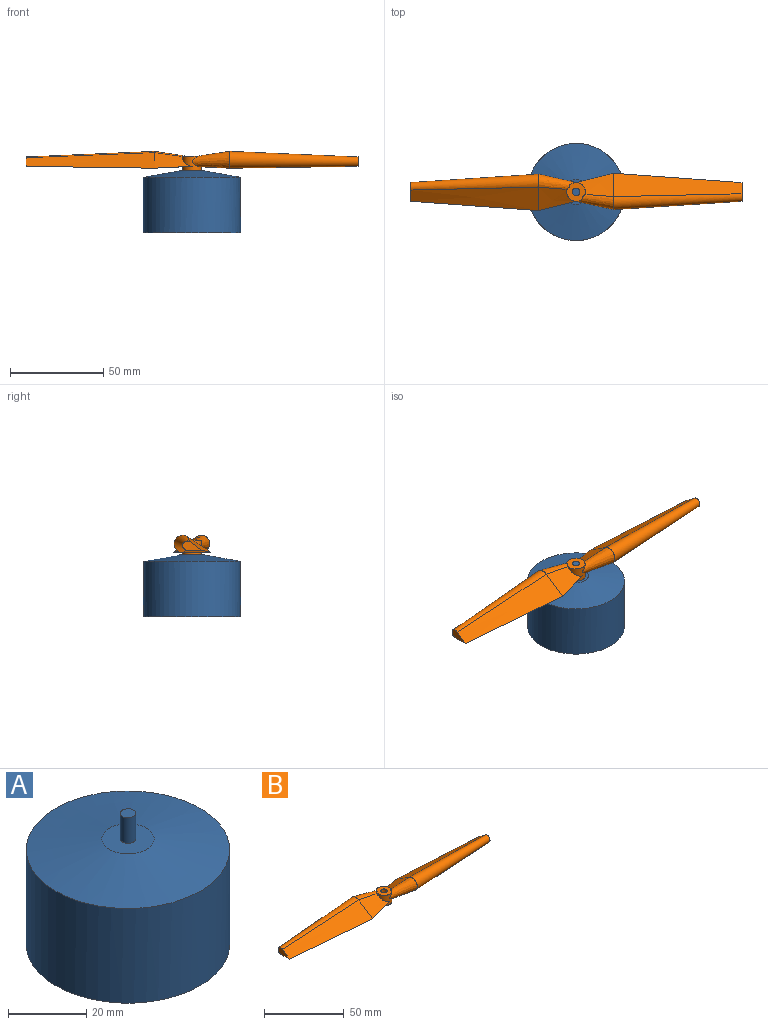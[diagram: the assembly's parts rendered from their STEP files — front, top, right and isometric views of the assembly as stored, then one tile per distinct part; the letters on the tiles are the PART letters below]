
ASSEMBLY  parts=2 mates=1
PART A: 6 faces, bbox 52x52x41 mm
  f0: cylinder r=26mm len=52mm, axis (0,0,-1), area 4834.2mm2, adj f1,f2
  f1: plane 52x52mm, normal (0,0,-1), area 2123.7mm2, adj f0
  f2: cone r=51mm half-angle=80deg, axis (0,0,-1), area 2014.5mm2, adj f0,f3
  f3: plane 13.34x13.34mm, normal (0,0,1), area 127.3mm2, adj f2,f4
  f4: cylinder r=2mm len=8mm, axis (0,0,-1), area 100.5mm2, adj f3,f5
  f5: plane 4x4mm, normal (0,0,1), area 12.6mm2, adj f4
PART B: 19 faces, bbox 178x20.2x10.8 mm
  f0: bspline ~20x12.52mm, area 194.1mm2, adj f1,f2,f4,f8
  f1: bspline ~20x9mm, area 243.5mm2, adj f0,f2,f5,f8,f17
  f2: plane 20.25x15.25mm, normal (-0.05,0,-1), area 192.6mm2, adj f0,f1,f6,f8
  f3: plane 10.09x5.09mm, normal (1,0,0), area 30.6mm2, adj f4,f5,f6
  f4: bspline ~68.9x12.52mm, area 775.2mm2, adj f0,f3,f5,f6
  f5: bspline ~68.9x9.01mm, area 904.5mm2, adj f1,f3,f4,f6
  f6: plane 68.9x15mm, normal (0.01,0,-1), area 775.2mm2, adj f2,f3,f4,f5
  f7: cylinder r=2mm len=8mm, axis (0,0,1), area 100.5mm2, adj f17,f18
  f8: cylinder r=5mm len=10mm, axis (0,0,-1), area 152.4mm2, adj f0,f1,f2,f9,f10,f11,f12,f17
  f9: cylinder r=5mm len=0.68mm, axis (0,0,-1), area 0.1mm2, adj f8,f11,f17
  f10: bspline ~20x12.52mm, area 194.1mm2, adj f8,f11,f12,f14
  f11: bspline ~20x9mm, area 243.5mm2, adj f8,f9,f10,f12,f15,f17
  f12: plane 20.16x15.16mm, normal (0.05,0,-1), area 192.6mm2, adj f8,f10,f11,f16
  f13: plane 10.09x5.09mm, normal (-1,0,0), area 30.6mm2, adj f14,f15,f16
  f14: bspline ~68.9x12.52mm, area 775.2mm2, adj f10,f13,f15,f16
  f15: bspline ~68.9x9.05mm, area 904.5mm2, adj f11,f13,f14,f16
  f16: plane 68.9x15mm, normal (-0.01,0,-1), area 775.2mm2, adj f12,f13,f14,f15
  f17: plane 10x10mm, normal (0,0,1), area 64.5mm2, adj f1,f7,f8,f9,f11
  f18: plane 10x10mm, normal (0,0,-1), area 66mm2, adj f7,f8
PLACE A at identity fixed
PLACE B t=(0,0,21.5)mm
MATE revolute B.f7 <-> A.f2  axis (0,0,-1) through (0,0,16.5)mm
